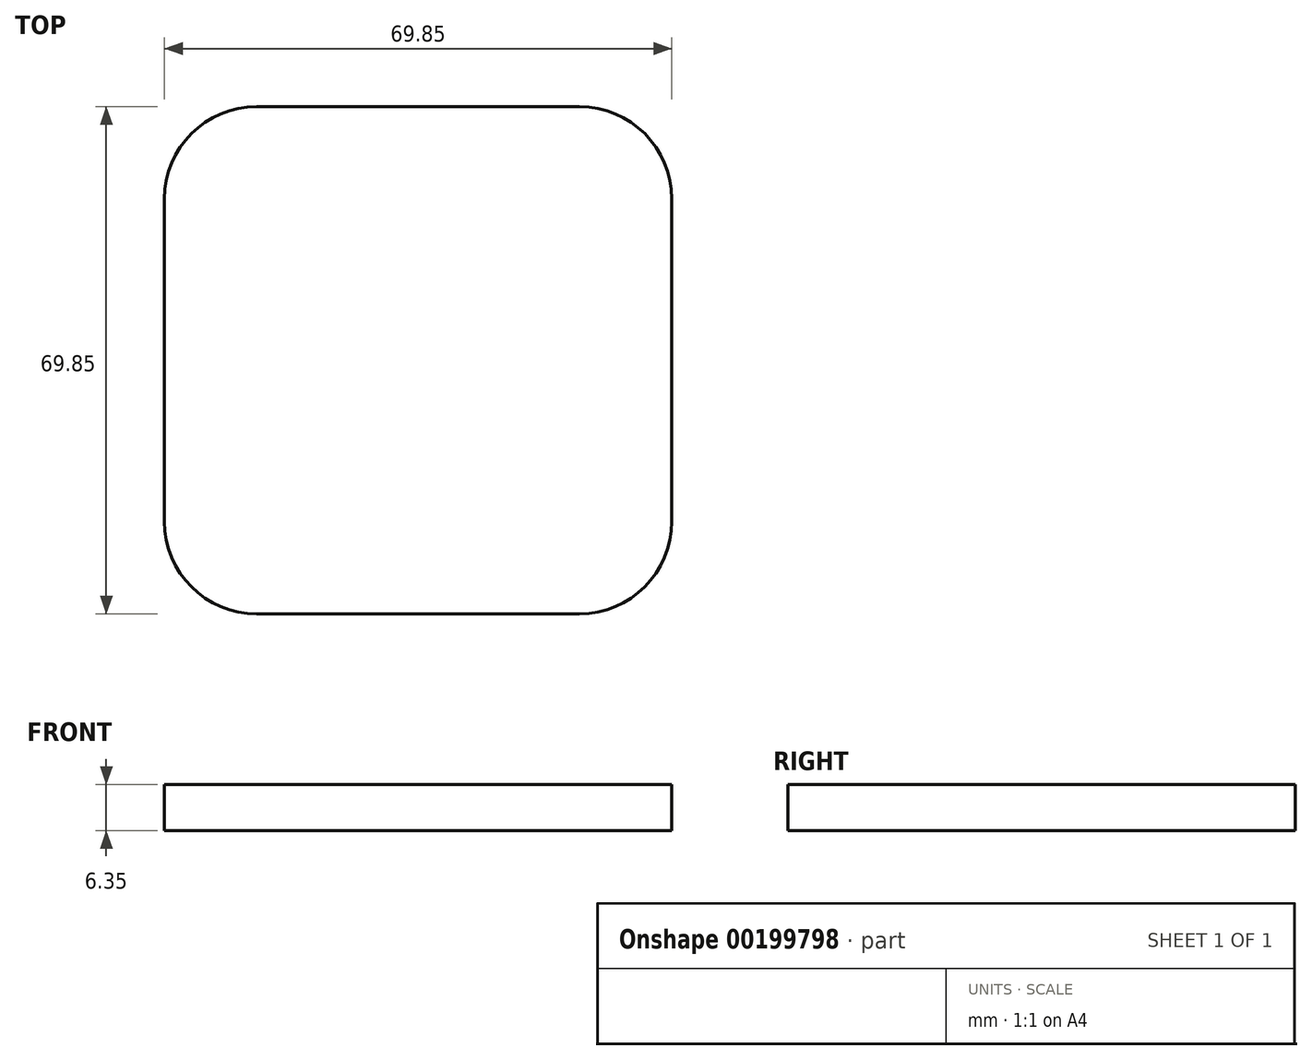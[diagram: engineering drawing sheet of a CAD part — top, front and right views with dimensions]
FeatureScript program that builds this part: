
annotation { "Feature Type Name" : "Feature", "Feature Type Description" : "" }
export const myFeature = defineFeature(function(context is Context, id is Id, definition is map)
    precondition{}
    {
        {
            var Q0;
            Q0=qCreatedBy(makeId("Top.planeOp"),FACE);
            var sketch = newSketch(context, id + "F0", { "sketchPlane" : qUnion([Q0])});
            skLineSegment(sketch, "E0.bottom", {"start": v(20.38, -85.51) * mm, "end": v(64.83, -85.51) * mm});
            skLineSegment(sketch, "E0.top", {"start": v(20.38, -15.66) * mm, "end": v(64.83, -15.66) * mm});
            skLineSegment(sketch, "E0.left", {"start": v(7.68, -72.81) * mm, "end": v(7.68, -28.36) * mm});
            skLineSegment(sketch, "E0.right", {"start": v(77.53, -72.81) * mm, "end": v(77.53, -28.36) * mm});
            skPoint(sketch, "E1.visualSharp", {"position": v(7.68, -85.51) * mm});
            skArc(sketch, "E1.filletArc", {"start": v(7.68, -72.81) * mm, "mid": v(11.4, -81.8) * mm, "end": v(20.38, -85.51) * mm});
            skPoint(sketch, "E2.visualSharp", {"position": v(77.53, -85.51) * mm});
            skArc(sketch, "E2.filletArc", {"start": v(64.83, -85.51) * mm, "mid": v(73.8, -81.8) * mm, "end": v(77.53, -72.81) * mm});
            skPoint(sketch, "E3.visualSharp", {"position": v(77.53, -15.66) * mm});
            skArc(sketch, "E3.filletArc", {"start": v(77.53, -28.36) * mm, "mid": v(73.8, -19.38) * mm, "end": v(64.83, -15.66) * mm});
            skPoint(sketch, "E4.visualSharp", {"position": v(7.68, -15.66) * mm});
            skArc(sketch, "E4.filletArc", {"start": v(20.38, -15.66) * mm, "mid": v(11.4, -19.38) * mm, "end": v(7.68, -28.36) * mm});
            skSolve(sketch);
        }
        {
            var Q0;
            Q0 = qSketchRegion(id + "F0", true);
            extrude(context, id + "F1", {"entities" : qUnion([Q0]), "depth" : 6.35 * mm});
        }
    });
